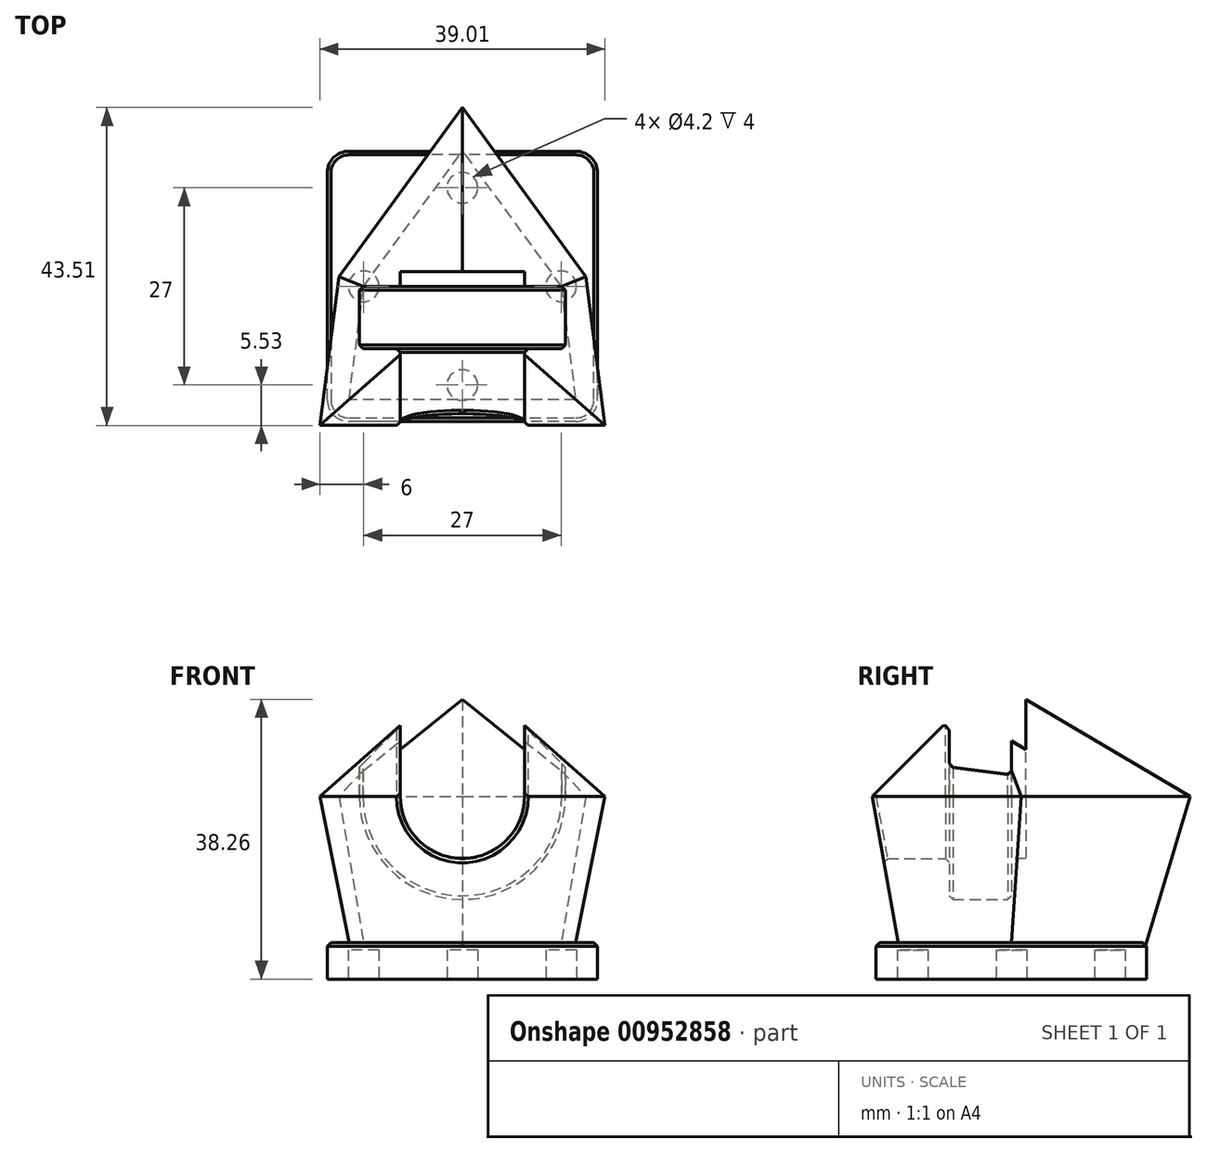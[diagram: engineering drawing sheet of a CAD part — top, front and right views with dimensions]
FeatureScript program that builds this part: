
annotation { "Feature Type Name" : "Feature", "Feature Type Description" : "" }
export const myFeature = defineFeature(function(context is Context, id is Id, definition is map)
    precondition{}
    {
        {
            var Q0;
            Q0=qCreatedBy(makeId("Top.planeOp"),FACE);
            var sketch = newSketch(context, id + "F0", { "sketchPlane" : qUnion([Q0])});
            skLineSegment(sketch, "E0.bottom", {"start": v(15.5, -18.5) * mm, "end": v(-15.5, -18.5) * mm});
            skLineSegment(sketch, "E0.top", {"start": v(15.5, 18.5) * mm, "end": v(-15.5, 18.5) * mm});
            skLineSegment(sketch, "E0.left", {"start": v(18.5, -15.5) * mm, "end": v(18.5, 15.5) * mm});
            skLineSegment(sketch, "E0.right", {"start": v(-18.5, -15.5) * mm, "end": v(-18.5, 15.5) * mm});
            skPoint(sketch, "E0.middle", {"position": v(0, 0) * mm});
            skPoint(sketch, "E1.visualSharp", {"position": v(-18.5, 18.5) * mm});
            skArc(sketch, "E1.filletArc", {"start": v(-15.5, 18.5) * mm, "mid": v(-17.62, 17.62) * mm, "end": v(-18.5, 15.5) * mm});
            skPoint(sketch, "E2.visualSharp", {"position": v(18.5, 18.5) * mm});
            skArc(sketch, "E2.filletArc", {"start": v(18.5, 15.5) * mm, "mid": v(17.62, 17.62) * mm, "end": v(15.5, 18.5) * mm});
            skPoint(sketch, "E3.visualSharp", {"position": v(18.5, -18.5) * mm});
            skArc(sketch, "E3.filletArc", {"start": v(15.5, -18.5) * mm, "mid": v(17.62, -17.62) * mm, "end": v(18.5, -15.5) * mm});
            skPoint(sketch, "E4.visualSharp", {"position": v(-18.5, -18.5) * mm});
            skArc(sketch, "E4.filletArc", {"start": v(-18.5, -15.5) * mm, "mid": v(-17.62, -17.62) * mm, "end": v(-15.5, -18.5) * mm});
            skCircle(sketch, "E5", {"center": v(0, 13.5) * mm, "radius": 2.1 * mm});
            skCircle(sketch, "E6.1.0", {"center": v(-13.5, 0) * mm, "radius": 2.1 * mm});
            skCircle(sketch, "E6.2.0", {"center": v(0, -13.5) * mm, "radius": 2.1 * mm});
            skCircle(sketch, "E6.3.0", {"center": v(13.5, 0) * mm, "radius": 2.1 * mm});
            skSolve(sketch);
        }
        {
            var Q0;
            Q0=makeQuery(id+"F0.imprint","IMPRINT",FACE,{"disambiguationData":[TD([[makeQuery(id+"F0.imprint","IMPRINT",EDGE,{"derivedFrom":sQuery(id+"F0.wireOp",EDGE,"E0.bottom")}),-1.0]])]});
            var Q1;
            Q1=makeQuery(id+"F0.imprint","IMPRINT",FACE,{"disambiguationData":[TD([[makeQuery(id+"F0.imprint","IMPRINT",EDGE,{"derivedFrom":sQuery(id+"F0.wireOp",EDGE,"E6.1.0")}),1.0]])]});
            var Q2;
            Q2=makeQuery(id+"F0.imprint","IMPRINT",FACE,{"disambiguationData":[TD([[makeQuery(id+"F0.imprint","IMPRINT",EDGE,{"derivedFrom":sQuery(id+"F0.wireOp",EDGE,"E5")}),1.0]])]});
            var Q3;
            Q3=makeQuery(id+"F0.imprint","IMPRINT",FACE,{"disambiguationData":[TD([[makeQuery(id+"F0.imprint","IMPRINT",EDGE,{"derivedFrom":sQuery(id+"F0.wireOp",EDGE,"E6.3.0")}),1.0]])]});
            var Q4;
            Q4=makeQuery(id+"F0.imprint","IMPRINT",FACE,{"disambiguationData":[TD([[makeQuery(id+"F0.imprint","IMPRINT",EDGE,{"derivedFrom":sQuery(id+"F0.wireOp",EDGE,"E6.2.0")}),1.0]])]});
            extrude(context, id + "F1", {"entities" : qUnion([Q0, Q1, Q2, Q3, Q4]), "depth" : 5 * mm, "offsetDistance" : 25 * mm});
        }
        {
            var Q0;
            Q0=makeQuery(id+"F0.imprint","IMPRINT",FACE,{"disambiguationData":[TD([[makeQuery(id+"F0.imprint","IMPRINT",EDGE,{"derivedFrom":sQuery(id+"F0.wireOp",EDGE,"E6.3.0")}),1.0]])]});
            var Q1;
            Q1=makeQuery(id+"F0.imprint","IMPRINT",FACE,{"disambiguationData":[TD([[makeQuery(id+"F0.imprint","IMPRINT",EDGE,{"derivedFrom":sQuery(id+"F0.wireOp",EDGE,"E5")}),1.0]])]});
            var Q2;
            Q2=makeQuery(id+"F0.imprint","IMPRINT",FACE,{"disambiguationData":[TD([[makeQuery(id+"F0.imprint","IMPRINT",EDGE,{"derivedFrom":sQuery(id+"F0.wireOp",EDGE,"E6.1.0")}),1.0]])]});
            var Q3;
            Q3=makeQuery(id+"F0.imprint","IMPRINT",FACE,{"disambiguationData":[TD([[makeQuery(id+"F0.imprint","IMPRINT",EDGE,{"derivedFrom":sQuery(id+"F0.wireOp",EDGE,"E6.2.0")}),1.0]])]});
            extrude(context, id + "F2", {"entities" : qUnion([Q0, Q1, Q2, Q3]), "operationType" : NewBodyOperationType.REMOVE, "depth" : 4 * mm, "offsetDistance" : 25 * mm});
        }
        {
            var Q0;
            Q0=makeQuery(id+"F1.opExtrude","CAP_FACE",FACE,{"disambiguationData":[OSD([sQuery(id+"F0.wireOp",EDGE,"E0.bottom"),sQuery(id+"F0.wireOp",EDGE,"E0.top"),sQuery(id+"F0.wireOp",EDGE,"E0.left"),sQuery(id+"F0.wireOp",EDGE,"E0.right"),sQuery(id+"F0.wireOp",EDGE,"E1.filletArc"),sQuery(id+"F0.wireOp",EDGE,"E2.filletArc"),sQuery(id+"F0.wireOp",EDGE,"E3.filletArc"),sQuery(id+"F0.wireOp",EDGE,"E4.filletArc")])],"isStart":false});
            var sketch = newSketch(context, id + "F3", { "sketchPlane" : qUnion([Q0])});
            skLineSegment(sketch, "E7", {"start": v(-15.5, -15.5) * mm, "end": v(-13.53, 0) * mm});
            skLineSegment(sketch, "E8", {"start": v(-13.53, 0) * mm, "end": v(0, 18.5) * mm});
            skLineSegment(sketch, "E9", {"start": v(0, 18.5) * mm, "end": v(13.5, 0) * mm});
            skLineSegment(sketch, "E10", {"start": v(13.5, 0) * mm, "end": v(15.5, -15.5) * mm});
            skLineSegment(sketch, "E11", {"start": v(15.5, -15.5) * mm, "end": v(-15.5, -15.5) * mm});
            skSolve(sketch);
        }
        {
            var Q0;
            Q0=makeQuery(id+"F3.imprint","IMPRINT",FACE,{"disambiguationData":[TD([[makeQuery(id+"F3.imprint","IMPRINT",EDGE,{"derivedFrom":sQuery(id+"F3.wireOp",EDGE,"E7")}),-1.0]])]});
            extrude(context, id + "F4", {"entities" : qUnion([Q0]), "operationType" : NewBodyOperationType.ADD, "depth" : 20 * mm, "offsetDistance" : 25 * mm, "hasDraft" : true, "draftAngle" : 10 * degree});
        }
        {
            var Q0;
            Q0=makeQuery(id+"F4.opExtrude","CAP_FACE",FACE,{"disambiguationData":[OSD([sQuery(id+"F3.wireOp",EDGE,"E7"),sQuery(id+"F3.wireOp",EDGE,"E8"),sQuery(id+"F3.wireOp",EDGE,"E9"),sQuery(id+"F3.wireOp",EDGE,"E10"),sQuery(id+"F3.wireOp",EDGE,"E11")])],"isStart":false});
            extrude(context, id + "F5", {"entities" : qUnion([Q0]), "operationType" : NewBodyOperationType.ADD, "depth" : 14 * mm, "offsetDistance" : 25 * mm, "hasDraft" : true, "draftAngle" : 45 * degree, "draftPullDirection" : true});
        }
        {
            var Q0;
            Q0=qCreatedBy(makeId("Front.planeOp"),FACE);
            var sketch = newSketch(context, id + "F6", { "sketchPlane" : qUnion([Q0])});
            skArc(sketch, "E12", {"start": v(-14.1, 25) * mm, "mid": v(0, 10.9) * mm, "end": v(14.1, 25) * mm});
            skLineSegment(sketch, "E13", {"start": v(14.1, 25) * mm, "end": v(14.1, 43.68) * mm});
            skLineSegment(sketch, "E14", {"start": v(-14.1, 25) * mm, "end": v(-14.1, 44.58) * mm});
            skLineSegment(sketch, "E15", {"start": v(-14.1, 44.58) * mm, "end": v(14.1, 43.68) * mm});
            skSolve(sketch);
        }
        {
            var Q0;
            Q0=makeQuery(id+"F6.imprint","IMPRINT",FACE,{"disambiguationData":[TD([[makeQuery(id+"F6.imprint","IMPRINT",EDGE,{"derivedFrom":sQuery(id+"F6.wireOp",EDGE,"E12")}),1.0]])]});
            extrude(context, id + "F7", {"entities" : qUnion([Q0]), "operationType" : NewBodyOperationType.REMOVE, "depth" : 8.5 * mm, "offsetDistance" : 25 * mm});
        }
        {
            var Q0;
            Q0=qCreatedBy(makeId("Front.planeOp"),FACE);
            var sketch = newSketch(context, id + "F8", { "sketchPlane" : qUnion([Q0])});
            skArc(sketch, "E16", {"start": v(-8.5, 25) * mm, "mid": v(0, 16.5) * mm, "end": v(8.5, 25) * mm});
            skLineSegment(sketch, "E17", {"start": v(8.5, 25) * mm, "end": v(8.5, 40.24) * mm});
            skLineSegment(sketch, "E18", {"start": v(-8.5, 25) * mm, "end": v(-8.5, 40.24) * mm});
            skLineSegment(sketch, "E19", {"start": v(-8.5, 40.24) * mm, "end": v(8.5, 40.24) * mm});
            skSolve(sketch);
        }
        {
            var Q0;
            Q0=makeQuery(id+"F8.imprint","IMPRINT",FACE,{"disambiguationData":[TD([[makeQuery(id+"F8.imprint","IMPRINT",EDGE,{"derivedFrom":sQuery(id+"F8.wireOp",EDGE,"E16")}),1.0]])]});
            extrude(context, id + "F9", {"entities" : qUnion([Q0]), "operationType" : NewBodyOperationType.REMOVE, "depth" : 25 * mm, "offsetDistance" : 25 * mm});
        }
        {
            var Q0;
            Q0=makeQuery(id+"F1.opExtrude","CAP_EDGE",EDGE,{"disambiguationData":[OSD([sQuery(id+"F0.wireOp",EDGE,"E0.right")])],"isStart":false});
            var Q1;
            Q1=makeQuery(id+"F9.boolean.opBoolean","INTERSECT",EDGE,{"derivedFrom":[makeQuery(id+"F7.boolean.opBoolean","COPY",FACE,{"derivedFrom":makeQuery(id+"F7.opExtrude","CAP_FACE",FACE,{"disambiguationData":[OSD([sQuery(id+"F6.wireOp",EDGE,"E12"),sQuery(id+"F6.wireOp",EDGE,"E13"),sQuery(id+"F6.wireOp",EDGE,"E14"),sQuery(id+"F6.wireOp",EDGE,"E15")])],"isStart":false})}),makeQuery(id+"F9.opExtrude","SWEPT_FACE",FACE,{"disambiguationData":[OSD([sQuery(id+"F8.wireOp",EDGE,"E16")])]})]});
            var Q2;
            Q2=makeQuery(id+"F7.boolean.opBoolean","COPY",EDGE,{"derivedFrom":makeQuery(id+"F7.opExtrude","CAP_EDGE",EDGE,{"disambiguationData":[OSD([sQuery(id+"F6.wireOp",EDGE,"E12")])],"isStart":true})});
            var Q3;
            Q3=makeQuery(id+"F7.boolean.opBoolean","COPY",EDGE,{"derivedFrom":makeQuery(id+"F7.opExtrude","CAP_EDGE",EDGE,{"disambiguationData":[OSD([sQuery(id+"F6.wireOp",EDGE,"E12")])],"isStart":false})});
            var Q4;
            Q4=makeQuery(id+"F9.boolean.opBoolean","INTERSECT",EDGE,{"derivedFrom":[makeQuery(id+"F4.opExtrude","SWEPT_FACE",FACE,{"disambiguationData":[OSD([sQuery(id+"F3.wireOp",EDGE,"E11")])]}),makeQuery(id+"F9.opExtrude","SWEPT_FACE",FACE,{"disambiguationData":[OSD([sQuery(id+"F8.wireOp",EDGE,"E16")])]})]});
            chamfer(context, id + "F10", {"entities" : qUnion([Q0, Q1, Q2, Q3, Q4]), "width" : 0.5 * mm, "tangentPropagation" : true});
        }
        {
            var Q0;
            Q0 = qSketchRegion(id + "F8", true);
            extrude(context, id + "F11", {"entities" : qUnion([Q0]), "operationType" : NewBodyOperationType.REMOVE, "oppositeDirection" : true, "depth" : 2 * mm, "offsetDistance" : 25 * mm});
        }
    });
